# Revit family: Deca_Acabamento para registro de pressão redonda_Deca You_4916.104.PQ
name_source: partatom
category: Plumbing Fixtures
units: mm (PartAtom-declared; Revit-internal decimal feet)

## family parameters
Cut with Voids When Loaded = No
Host = Face
Part Type = Normal
Room Calculation Point = No
Round Connector Dimension = Use Radius
Shared = No

## types (7) — shared parameters
Acompanha o Produto = Mecanismo
Aprovado por = quattroD
Atendimento ao Cliente = 0800-0117073
Categoria = Acabamento de Registro
Composição Básica = Liga de Cobre (Latão),Plásticos de Engenharia, Aço Inoxidavel e Elastômeros
Consumo = -
Cor Secundária = -
Criado por = quattroD
Default Elevation = 1.1 m
Itens de Instalação = -
Linha = Deca You
Manufacturer = DECA
Norma = Não possui
Pressão máx. funcionamento = -
Pressão mín. Aquec. Acúmulo = -
Pressão mín. Aquec. Passagem = -
Pressão mín. funcionamento = -
Saída de Esgoto = -
Segmento = Luxo
Tipo de dispositivo economizador = -
Tipo de mecanismo utilizado = MVC  - 1/2 de volta
Tipo de rosca de entrada = -
Tipo de rosca de saída = -
URL = www.deca.com.br
Vazão na Pressão máx. (L/min) = -
Vazão na Pressão mín. (L/min) = -
zero-valued in all types: CWFU, Diâmetro Ponto de Esgoto, Diâmetro Água Fria, Peso Líquido (Kg), Raio Ponto de Esgoto, Raio Água Fria, WFU

## per-type parameters (varying)
| type | Cor Principal | Código Pai | Material | Model |
| 4916.C104.PQ_Cromado | Cromado | 4916.C104.PQ | Deca_Cromado | 4916.C104.PQ |
| 4916.BL104.PQ.MT_Black Matte | Black Matte | 4916.BL104.PQ.MT | Deca_Black Matte | 4916.BL104.PQ.MT |
| 4916.GF104.PQ.MT_Grafite | Antracite Dark | 4916.GF104.PQ.MT | Deca_Grafite | 4916.GF104.PQ.MT |
| 4916.INX104.PQ_Inox | Inox | 4916.INX104.PQ | Deca_Inox | 4916.INX104.PQ |
| 4916.MR104.PQ.MT_Brown Matte | BROWN MATTE | 4916.MR104.PQ.MT | Deca_Brown Matte | 4916.MR104.PQ.MT |
| 4916.SM104.PQ.MT_Summer Gold | SUMMER GOLD | 4916.SM104.PQ.MT | Deca_Summer Gold | 4916.SM104.PQ.MT |
| 4916.BR104.PQ.MT_Dynamic White | Dynamic White | 4916.BR104.PQ.MT | Deca_Dynamic White | 4916.BR104.PQ.MT |

## geometry (parser evidence)
native form markers: Sweep x2
no freeform markers — native parametric forms only
